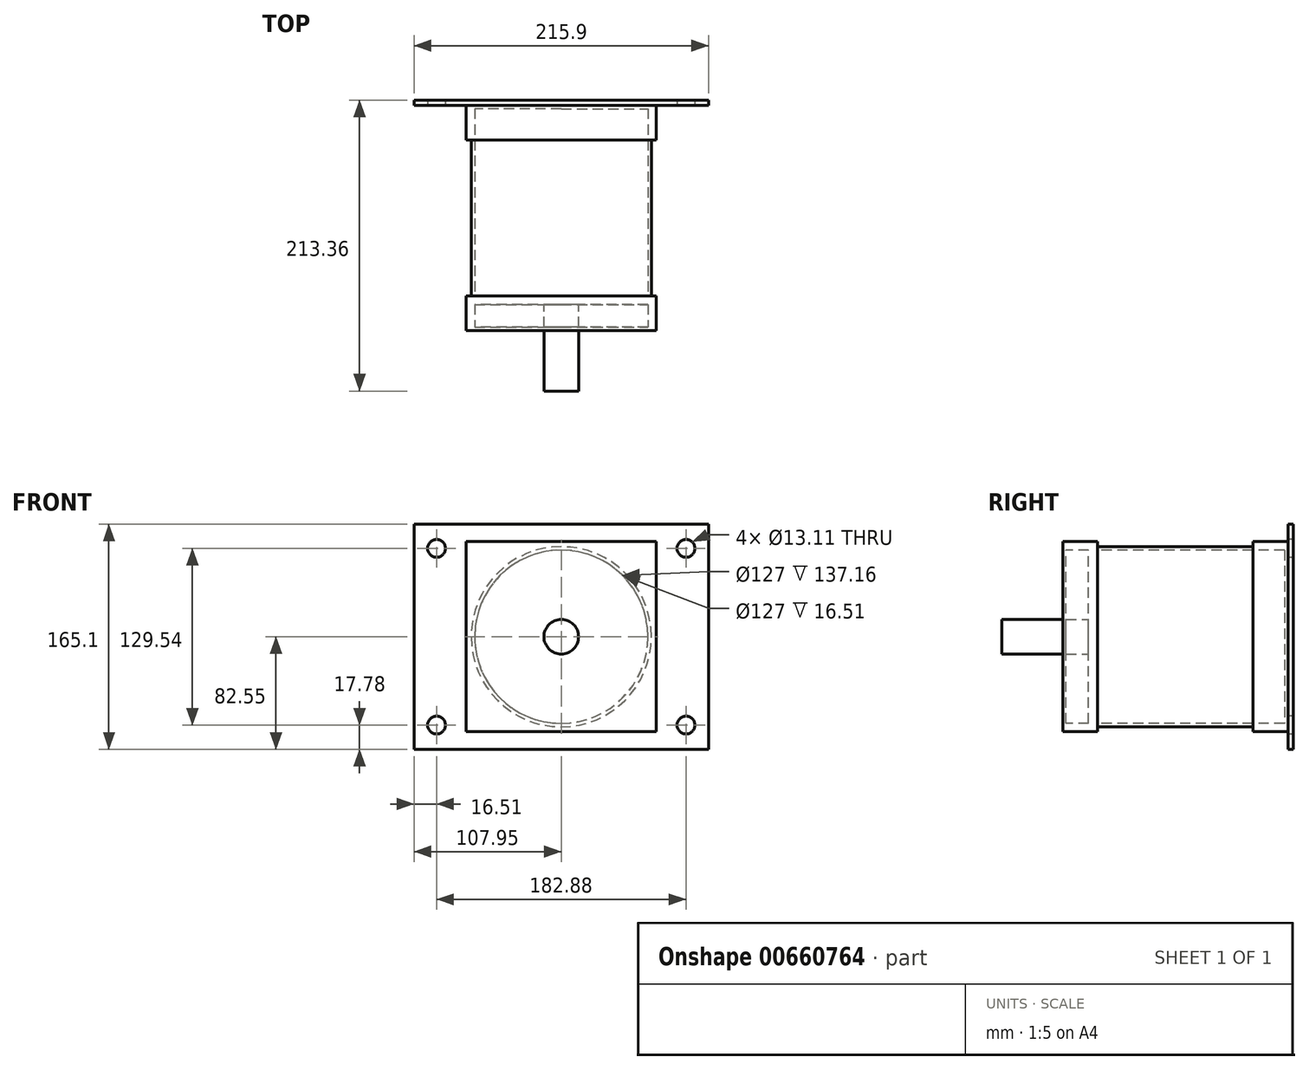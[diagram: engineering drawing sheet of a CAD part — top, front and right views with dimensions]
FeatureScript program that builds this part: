
annotation { "Feature Type Name" : "Feature", "Feature Type Description" : "" }
export const myFeature = defineFeature(function(context is Context, id is Id, definition is map)
    precondition{}
    {
        {
            var Q0;
            Q0=qCreatedBy(makeId("Front.planeOp"),FACE);
            var sketch = newSketch(context, id + "F0", { "sketchPlane" : qUnion([Q0])});
            skLineSegment(sketch, "E0.bottom", {"start": v(-69.67, 69.67) * mm, "end": v(69.67, 69.67) * mm});
            skLineSegment(sketch, "E0.top", {"start": v(-69.67, -69.67) * mm, "end": v(69.67, -69.67) * mm});
            skLineSegment(sketch, "E0.left", {"start": v(-69.67, 69.67) * mm, "end": v(-69.67, -69.67) * mm});
            skLineSegment(sketch, "E0.right", {"start": v(69.67, 69.67) * mm, "end": v(69.67, -69.67) * mm});
            skSolve(sketch);
        }
        {
            var Q0;
            Q0 = qSketchRegion(id + "F0", true);
            extrude(context, id + "F1", {"entities" : qUnion([Q0]), "depth" : 165.1 * mm, "offsetDistance" : 25.4 * mm});
        }
        {
            var Q0;
            Q0=makeQuery(id+"F1.opExtrude","CAP_FACE",FACE,{"disambiguationData":[OSD([sQuery(id+"F0.wireOp",EDGE,"E0.bottom"),sQuery(id+"F0.wireOp",EDGE,"E0.top"),sQuery(id+"F0.wireOp",EDGE,"E0.left"),sQuery(id+"F0.wireOp",EDGE,"E0.right")])],"isStart":false});
            cPlane(context, id + "F2", {"entities" : qUnion([Q0]), "cplaneType" : CPlaneType.OFFSET, "offset" : 25.4 * mm, "oppositeDirection" : true, "width" : 152.4 * mm, "height" : 152.4 * mm});
        }
        {
            var Q0;
            Q0=qCreatedBy(id+"F2.planeOp",FACE);
            var sketch = newSketch(context, id + "F3", { "sketchPlane" : qUnion([Q0])});
            skCircle(sketch, "E1", {"center": v(0, 0) * mm, "radius": 66.04 * mm});
            skLineSegment(sketch, "E2.0", {"start": v(-69.67, 69.67) * mm, "end": v(69.67, 69.67) * mm});
            skLineSegment(sketch, "E3.0", {"start": v(-69.67, 69.67) * mm, "end": v(-69.67, -69.67) * mm});
            skLineSegment(sketch, "E4.0", {"start": v(69.67, 69.67) * mm, "end": v(69.67, -69.67) * mm});
            skLineSegment(sketch, "E5.0", {"start": v(-69.67, -69.67) * mm, "end": v(69.67, -69.67) * mm});
            skSolve(sketch);
        }
        {
            var Q0;
            Q0 = qSketchRegion(id + "F3", true);
            extrude(context, id + "F4", {"entities" : qUnion([Q0]), "operationType" : NewBodyOperationType.REMOVE, "oppositeDirection" : true, "depth" : 114.3 * mm, "offsetDistance" : 25.4 * mm});
        }
        {
            var Q0;
            Q0=makeQuery(id+"F1.opExtrude","CAP_FACE",FACE,{"disambiguationData":[OSD([sQuery(id+"F0.wireOp",EDGE,"E0.bottom"),sQuery(id+"F0.wireOp",EDGE,"E0.top"),sQuery(id+"F0.wireOp",EDGE,"E0.left"),sQuery(id+"F0.wireOp",EDGE,"E0.right")])],"isStart":false});
            var sketch = newSketch(context, id + "F5", { "sketchPlane" : qUnion([Q0])});
            skCircle(sketch, "E6", {"center": v(0, 0) * mm, "radius": 63.5 * mm});
            skSolve(sketch);
        }
        {
            var Q0;
            Q0 = qSketchRegion(id + "F5", true);
            extrude(context, id + "F6", {"entities" : qUnion([Q0]), "operationType" : NewBodyOperationType.REMOVE, "endBound" : BoundingType.THROUGH_ALL, "oppositeDirection" : true, "depth" : 25.4 * mm, "offsetDistance" : 25.4 * mm});
        }
        {
            var Q0;
            Q0=makeQuery(id+"F1.opExtrude","CAP_FACE",FACE,{"disambiguationData":[OSD([sQuery(id+"F0.wireOp",EDGE,"E0.bottom"),sQuery(id+"F0.wireOp",EDGE,"E0.top"),sQuery(id+"F0.wireOp",EDGE,"E0.left"),sQuery(id+"F0.wireOp",EDGE,"E0.right")])],"isStart":true});
            var sketch = newSketch(context, id + "F7", { "sketchPlane" : qUnion([Q0])});
            skCircle(sketch, "E7", {"center": v(0, 0) * mm, "radius": 63.5 * mm});
            skSolve(sketch);
        }
        {
            var Q0;
            Q0 = qSketchRegion(id + "F7", true);
            extrude(context, id + "F8", {"entities" : qUnion([Q0]), "operationType" : NewBodyOperationType.ADD, "oppositeDirection" : true, "depth" : 2.54 * mm, "offsetDistance" : 25.4 * mm});
        }
        {
            var Q0;
            Q0=qCreatedBy(id+"F2.planeOp",FACE);
            var sketch = newSketch(context, id + "F9", { "sketchPlane" : qUnion([Q0])});
            skCircle(sketch, "E8", {"center": v(0, 0) * mm, "radius": 63.5 * mm});
            skSolve(sketch);
        }
        {
            var Q0;
            Q0 = qSketchRegion(id + "F9", true);
            extrude(context, id + "F10", {"entities" : qUnion([Q0]), "operationType" : NewBodyOperationType.ADD, "depth" : 6.35 * mm, "offsetDistance" : 25.4 * mm});
        }
        {
            var Q0;
            Q0=makeQuery(id+"F10.opExtrude","CAP_FACE",FACE,{"disambiguationData":[OSD([sQuery(id+"F9.wireOp",EDGE,"E8")])],"isStart":false});
            var sketch = newSketch(context, id + "F11", { "sketchPlane" : qUnion([Q0])});
            skCircle(sketch, "E9", {"center": v(0, 0) * mm, "radius": 12.7 * mm});
            skSolve(sketch);
        }
        {
            var Q0;
            Q0 = qSketchRegion(id + "F11", true);
            extrude(context, id + "F12", {"entities" : qUnion([Q0]), "operationType" : NewBodyOperationType.ADD, "depth" : 63.5 * mm, "offsetDistance" : 25.4 * mm});
        }
        {
            var Q0;
            Q0=makeQuery(id+"F8.boolean.opBoolean","MERGE",FACE,{"derivedFrom":[makeQuery(id+"F1.opExtrude","CAP_FACE",FACE,{"disambiguationData":[OSD([sQuery(id+"F0.wireOp",EDGE,"E0.bottom"),sQuery(id+"F0.wireOp",EDGE,"E0.top"),sQuery(id+"F0.wireOp",EDGE,"E0.left"),sQuery(id+"F0.wireOp",EDGE,"E0.right")])],"isStart":true}),makeQuery(id+"F8.opExtrude","CAP_FACE",FACE,{"disambiguationData":[OSD([sQuery(id+"F7.wireOp",EDGE,"E7")])],"isStart":true})]});
            var sketch = newSketch(context, id + "F13", { "sketchPlane" : qUnion([Q0])});
            skLineSegment(sketch, "E10.bottom", {"start": v(-107.95, 82.55) * mm, "end": v(107.95, 82.55) * mm});
            skLineSegment(sketch, "E10.top", {"start": v(-107.95, -82.55) * mm, "end": v(107.95, -82.55) * mm});
            skLineSegment(sketch, "E10.left", {"start": v(-107.95, 82.55) * mm, "end": v(-107.95, -82.55) * mm});
            skLineSegment(sketch, "E10.right", {"start": v(107.95, 82.55) * mm, "end": v(107.95, -82.55) * mm});
            skSolve(sketch);
        }
        {
            var Q0;
            Q0 = qSketchRegion(id + "F13", true);
            extrude(context, id + "F14", {"entities" : qUnion([Q0]), "operationType" : NewBodyOperationType.ADD, "depth" : 3.8 * mm, "offsetDistance" : 25.4 * mm});
        }
        {
            var Q0;
            Q0=makeQuery(id+"F14.opExtrude","CAP_FACE",FACE,{"disambiguationData":[OSD([sQuery(id+"F13.wireOp",EDGE,"E10.bottom"),sQuery(id+"F13.wireOp",EDGE,"E10.top"),sQuery(id+"F13.wireOp",EDGE,"E10.left"),sQuery(id+"F13.wireOp",EDGE,"E10.right")])],"isStart":true});
            var sketch = newSketch(context, id + "F15", { "sketchPlane" : qUnion([Q0])});
            skPoint(sketch, "E11", {"position": v(91.44, 64.77) * mm});
            skPoint(sketch, "E12", {"position": v(91.44, -64.77) * mm});
            skLineSegment(sketch, "E13", {"start": v(0, 130.52) * mm, "end": v(0, -123.57) * mm, "construction": true});
            skPoint(sketch, "E14.MirrorP", {"position": v(-91.44, -64.77) * mm});
            skPoint(sketch, "E15.MirrorP", {"position": v(-91.44, 64.77) * mm});
            skSolve(sketch);
        }
        {
            var Q0;
            Q0=sQuery(id+"F15.wireOp",VERTEX,"E11");
            var Q1;
            Q1=sQuery(id+"F15.wireOp",VERTEX,"E12");
            var Q2;
            Q2=sQuery(id+"F15.wireOp",VERTEX,"E15.MirrorP");
            var Q3;
            Q3=sQuery(id+"F15.wireOp",VERTEX,"E14.MirrorP");
            var Q4;
            Q4=makeQuery(id+"F1.opExtrude","SWEPT_BODY",BODY,{"disambiguationData":[OSD([sQuery(id+"F0.wireOp",EDGE,"E0.bottom"),sQuery(id+"F0.wireOp",EDGE,"E0.top"),sQuery(id+"F0.wireOp",EDGE,"E0.left"),sQuery(id+"F0.wireOp",EDGE,"E0.right")])]});
            hole(context, id + "F16", {"style" : HoleStyle.SIMPLE, "endStyle" : HoleEndStyle.THROUGH, "standardTappedOrClearance" : lookupTablePath({ "standard" : "ANSI", "fit" : "Close", "size" : "1/2", "type" : "Clearance" }), "standardBlindInLast" : lookupTablePath({ "fit" : "Close", "standard" : "ANSI", "size" : "1/2", "type" : "Clearance" }), "holeDiameter" : 13.1 * mm, "majorDiameter" : 6.35 * mm, "isTappedThrough" : true, "tappedDepth" : 12.7 * mm, "tapClearance" : 3, "locations" : qUnion([Q0, Q1, Q2, Q3]), "scope" : qUnion([Q4])});
        }
        {
            var Q0;
            Q0=makeQuery(id+"F1.opExtrude","CAP_FACE",FACE,{"disambiguationData":[OSD([sQuery(id+"F0.wireOp",EDGE,"E0.bottom"),sQuery(id+"F0.wireOp",EDGE,"E0.top"),sQuery(id+"F0.wireOp",EDGE,"E0.left"),sQuery(id+"F0.wireOp",EDGE,"E0.right")])],"isStart":false});
            var sketch = newSketch(context, id + "F17", { "sketchPlane" : qUnion([Q0])});
            skCircle(sketch, "E16.0", {"center": v(0, 0) * mm, "radius": 12.7 * mm});
            skCircle(sketch, "E17.0", {"center": v(0, 0) * mm, "radius": 63.5 * mm});
            skSolve(sketch);
        }
        {
            var Q0;
            Q0 = qSketchRegion(id + "F17", true);
            extrude(context, id + "F18", {"entities" : qUnion([Q0]), "operationType" : NewBodyOperationType.ADD, "oppositeDirection" : true, "depth" : 2.54 * mm, "offsetDistance" : 25.4 * mm});
        }
    });
